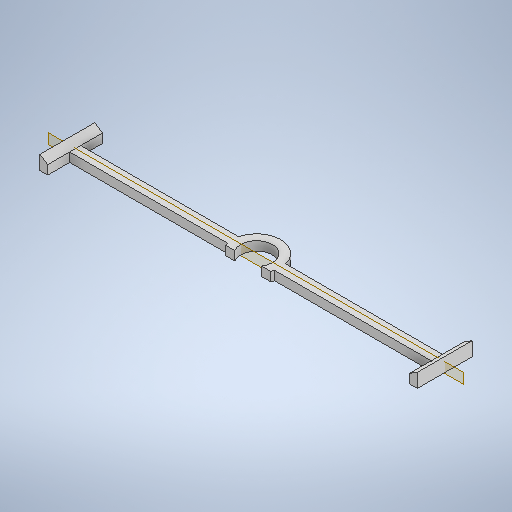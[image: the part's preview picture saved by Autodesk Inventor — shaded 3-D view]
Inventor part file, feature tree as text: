
AUTODESK INVENTOR PART (.ipt)
format: ipt  version: 2025.1 (Build 291241000, 241)  size: 304,128 bytes
history: native  units: mm
features: extrude x4, sketch x4, plane x1
ambient origin geometry x8: Origin, YZ Plane, XZ Plane, XY Plane, X Axis, Y Axis, Z Axis, Center Point
bodies: Volumenkörper1 (feature_tree)
feature tree (9):
  extrude  "Extrusion1"  Depth=2.85mm
  plane  "Arbeitsebene1"
  extrude  "Extrusion2"  Depth=2.85mm
  extrude  "Extrusion3"  Depth=19.7mm
  extrude  "Extrusion4"  Depth=3.25mm TaperAngle=0.0deg
  sketch  "Skizze1"  dims[d0=135.6mm d1=4.0mm d2=3.25mm d3=0.0mm d4=2.85mm]
  sketch  "Skizze2"  dims[d5=1.75mm d6=2.85mm]
  sketch  "Skizze3"  dims[d7=19.7mm d8=0.0mm d9=15.15mm]
  sketch  "Skizze4"  dims[d10=0.0mm d11=0.0mm d15=3.25mm d16=0.0mm d27=11.3mm d28=17.3mm d29=3.0mm d30=17.3mm d17=0.5mm d18=0.872665mm]
